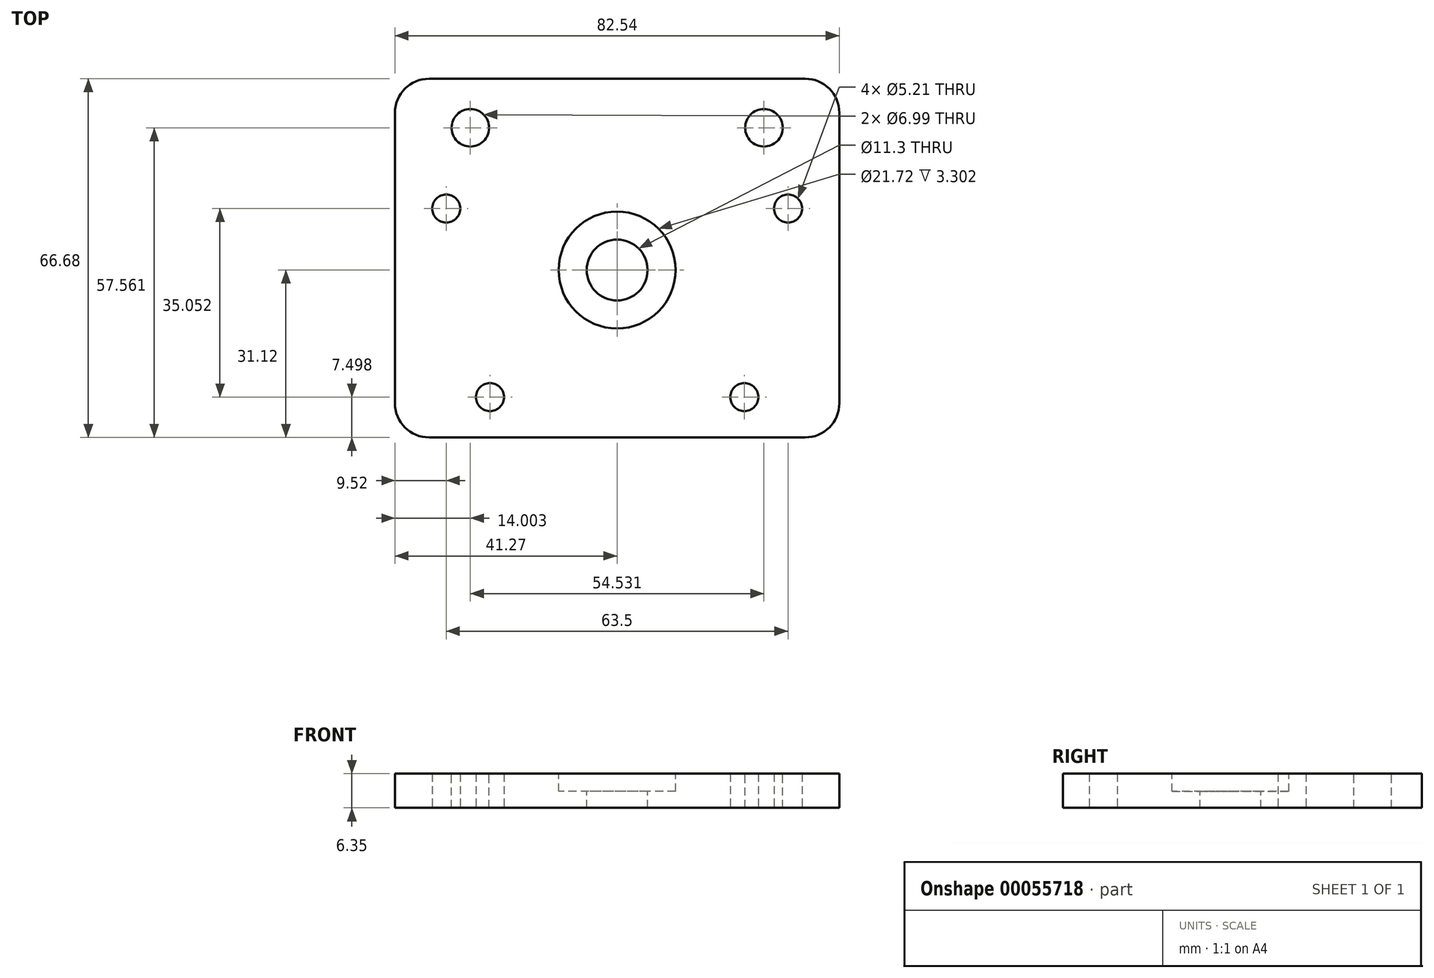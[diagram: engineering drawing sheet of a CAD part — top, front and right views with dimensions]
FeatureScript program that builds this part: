
annotation { "Feature Type Name" : "Feature", "Feature Type Description" : "" }
export const myFeature = defineFeature(function(context is Context, id is Id, definition is map)
    precondition{}
    {
        {
            var Q0;
            Q0=qCreatedBy(makeId("Top.planeOp"),FACE);
            var sketch = newSketch(context, id + "F0", { "sketchPlane" : qUnion([Q0])});
            skLineSegment(sketch, "E0.bottom", {"start": v(-23.62, 23.62) * mm, "end": v(23.62, 23.62) * mm});
            skLineSegment(sketch, "E0.top", {"start": v(-23.62, -23.62) * mm, "end": v(23.62, -23.62) * mm});
            skLineSegment(sketch, "E0.left", {"start": v(-23.62, 23.62) * mm, "end": v(-23.62, -23.62) * mm});
            skLineSegment(sketch, "E0.right", {"start": v(23.62, 23.62) * mm, "end": v(23.62, -23.62) * mm});
            skSolve(sketch);
        }
        {
            var Q0;
            Q0=qCreatedBy(makeId("Top.planeOp"),FACE);
            var sketch = newSketch(context, id + "F1", { "sketchPlane" : qUnion([Q0])});
            skLineSegment(sketch, "E1.bottom", {"start": v(-41.28, 35.56) * mm, "end": v(41.28, 35.56) * mm});
            skLineSegment(sketch, "E1.top", {"start": v(-41.28, -31.12) * mm, "end": v(41.28, -31.12) * mm});
            skLineSegment(sketch, "E1.left", {"start": v(-41.28, 35.56) * mm, "end": v(-41.28, -31.12) * mm});
            skLineSegment(sketch, "E1.right", {"start": v(41.28, 35.56) * mm, "end": v(41.28, -31.12) * mm});
            skSolve(sketch);
        }
        {
            var Q0;
            Q0=makeQuery(id+"F1.imprint","IMPRINT",FACE,{"disambiguationData":[TD([[makeQuery(id+"F1.imprint","IMPRINT",EDGE,{"derivedFrom":sQuery(id+"F1.wireOp",EDGE,"E1.bottom")}),-1.0]])]});
            extrude(context, id + "F2", {"entities" : qUnion([Q0]), "depth" : 6.35 * mm});
        }
        {
            var Q0;
            Q0=makeQuery(id+"F2.opExtrude","CAP_FACE",FACE,{"disambiguationData":[OSD([sQuery(id+"F1.wireOp",EDGE,"E1.bottom"),sQuery(id+"F1.wireOp",EDGE,"E1.top"),sQuery(id+"F1.wireOp",EDGE,"E1.left"),sQuery(id+"F1.wireOp",EDGE,"E1.right")])],"isStart":false});
            var sketch = newSketch(context, id + "F3", { "sketchPlane" : qUnion([Q0])});
            skPoint(sketch, "E2", {"position": v(0, 0) * mm});
            skSolve(sketch);
        }
        {
            var Q0;
            Q0=sQuery(id+"F3.wireOp",VERTEX,"E2");
            var Q1;
            Q1=makeQuery(id+"F2.opExtrude","SWEPT_BODY",BODY,{"disambiguationData":[OSD([sQuery(id+"F1.wireOp",EDGE,"E1.bottom"),sQuery(id+"F1.wireOp",EDGE,"E1.top"),sQuery(id+"F1.wireOp",EDGE,"E1.left"),sQuery(id+"F1.wireOp",EDGE,"E1.right")])]});
            hole(context, id + "F4", {"style" : HoleStyle.C_BORE, "holeDiameter" : 11.3 * mm, "cBoreDiameter" : 21.72 * mm, "cBoreDepth" : 3.3 * mm, "endStyle" : HoleEndStyle.THROUGH, "locations" : qUnion([Q0]), "scope" : qUnion([Q1])});
        }
        {
            var Q0;
            Q0=makeQuery(id+"F2.opExtrude","CAP_FACE",FACE,{"disambiguationData":[OSD([sQuery(id+"F1.wireOp",EDGE,"E1.bottom"),sQuery(id+"F1.wireOp",EDGE,"E1.top"),sQuery(id+"F1.wireOp",EDGE,"E1.left"),sQuery(id+"F1.wireOp",EDGE,"E1.right")])],"isStart":false});
            var sketch = newSketch(context, id + "F5", { "sketchPlane" : qUnion([Q0])});
            skCircle(sketch, "E3", {"center": v(-27.27, 26.44) * mm, "radius": 3.5 * mm});
            skCircle(sketch, "E4", {"center": v(27.26, 26.44) * mm, "radius": 3.5 * mm});
            skSolve(sketch);
        }
        {
            var Q0;
            Q0=sQuery(id+"F5.wireOp",VERTEX,"E3.center");
            var Q1;
            Q1=makeQuery(id+"F2.opExtrude","SWEPT_BODY",BODY,{"disambiguationData":[OSD([sQuery(id+"F1.wireOp",EDGE,"E1.bottom"),sQuery(id+"F1.wireOp",EDGE,"E1.top"),sQuery(id+"F1.wireOp",EDGE,"E1.left"),sQuery(id+"F1.wireOp",EDGE,"E1.right")])]});
            hole(context, id + "F6", {"style" : HoleStyle.SIMPLE, "holeDiameter" : 7 * mm, "endStyle" : HoleEndStyle.THROUGH, "locations" : qUnion([Q0]), "scope" : qUnion([Q1])});
        }
        {
            var Q0;
            Q0=sQuery(id+"F5.wireOp",VERTEX,"E4.center");
            var Q1;
            Q1=makeQuery(id+"F2.opExtrude","SWEPT_BODY",BODY,{"disambiguationData":[OSD([sQuery(id+"F1.wireOp",EDGE,"E1.bottom"),sQuery(id+"F1.wireOp",EDGE,"E1.top"),sQuery(id+"F1.wireOp",EDGE,"E1.left"),sQuery(id+"F1.wireOp",EDGE,"E1.right")])]});
            hole(context, id + "F7", {"style" : HoleStyle.SIMPLE, "holeDiameter" : 7 * mm, "endStyle" : HoleEndStyle.THROUGH, "locations" : qUnion([Q0]), "scope" : qUnion([Q1])});
        }
        {
            var Q0;
            Q0=sQuery(id+"F0.wireOp",VERTEX,"E0.right.end");
            var Q1;
            Q1=sQuery(id+"F0.wireOp",VERTEX,"E0.left.end");
            var Q2;
            Q2=makeQuery(id+"F2.opExtrude","SWEPT_BODY",BODY,{"disambiguationData":[OSD([sQuery(id+"F1.wireOp",EDGE,"E1.bottom"),sQuery(id+"F1.wireOp",EDGE,"E1.top"),sQuery(id+"F1.wireOp",EDGE,"E1.left"),sQuery(id+"F1.wireOp",EDGE,"E1.right")])]});
            hole(context, id + "F8", {"style" : HoleStyle.SIMPLE, "holeDiameter" : 5.2 * mm, "endStyle" : HoleEndStyle.THROUGH, "oppositeDirection" : true, "locations" : qUnion([Q0, Q1]), "scope" : qUnion([Q2])});
        }
        {
            var Q0;
            Q0=makeQuery(id+"F2.opExtrude","SWEPT_EDGE",EDGE,{"disambiguationData":[OSD([sQuery(id+"F1.wireOp",EDGE,"E1.top"),sQuery(id+"F1.wireOp",EDGE,"E1.left")])]});
            var Q1;
            Q1=makeQuery(id+"F2.opExtrude","SWEPT_EDGE",EDGE,{"disambiguationData":[OSD([sQuery(id+"F1.wireOp",EDGE,"E1.top"),sQuery(id+"F1.wireOp",EDGE,"E1.right")])]});
            var Q2;
            Q2=makeQuery(id+"F2.opExtrude","SWEPT_EDGE",EDGE,{"disambiguationData":[OSD([sQuery(id+"F1.wireOp",EDGE,"E1.bottom"),sQuery(id+"F1.wireOp",EDGE,"E1.right")])]});
            var Q3;
            Q3=makeQuery(id+"F2.opExtrude","SWEPT_EDGE",EDGE,{"disambiguationData":[OSD([sQuery(id+"F1.wireOp",EDGE,"E1.bottom"),sQuery(id+"F1.wireOp",EDGE,"E1.left")])]});
            fillet(context, id + "F9", {"entities" : qUnion([Q0, Q1, Q2, Q3]), "radius" : 6.35 * mm, "tangentPropagation" : true, "allowEdgeOverflow" : false});
        }
        {
            var Q0;
            Q0=qCreatedBy(makeId("Top.planeOp"),FACE);
            var sketch = newSketch(context, id + "F10", { "sketchPlane" : qUnion([Q0])});
            skLineSegment(sketch, "E5", {"start": v(-31.75, 11.43) * mm, "end": v(31.75, 11.43) * mm});
            skSolve(sketch);
        }
        {
            var Q0;
            Q0=sQuery(id+"F10.wireOp",VERTEX,"E5.start");
            var Q1;
            Q1=sQuery(id+"F10.wireOp",VERTEX,"E5.end");
            var Q2;
            Q2=makeQuery(id+"F2.opExtrude","SWEPT_BODY",BODY,{"disambiguationData":[OSD([sQuery(id+"F1.wireOp",EDGE,"E1.bottom"),sQuery(id+"F1.wireOp",EDGE,"E1.top"),sQuery(id+"F1.wireOp",EDGE,"E1.left"),sQuery(id+"F1.wireOp",EDGE,"E1.right")])]});
            hole(context, id + "F11", {"style" : HoleStyle.SIMPLE, "holeDiameter" : 5.2 * mm, "endStyle" : HoleEndStyle.THROUGH, "oppositeDirection" : true, "locations" : qUnion([Q0, Q1]), "scope" : qUnion([Q2])});
        }
    });
